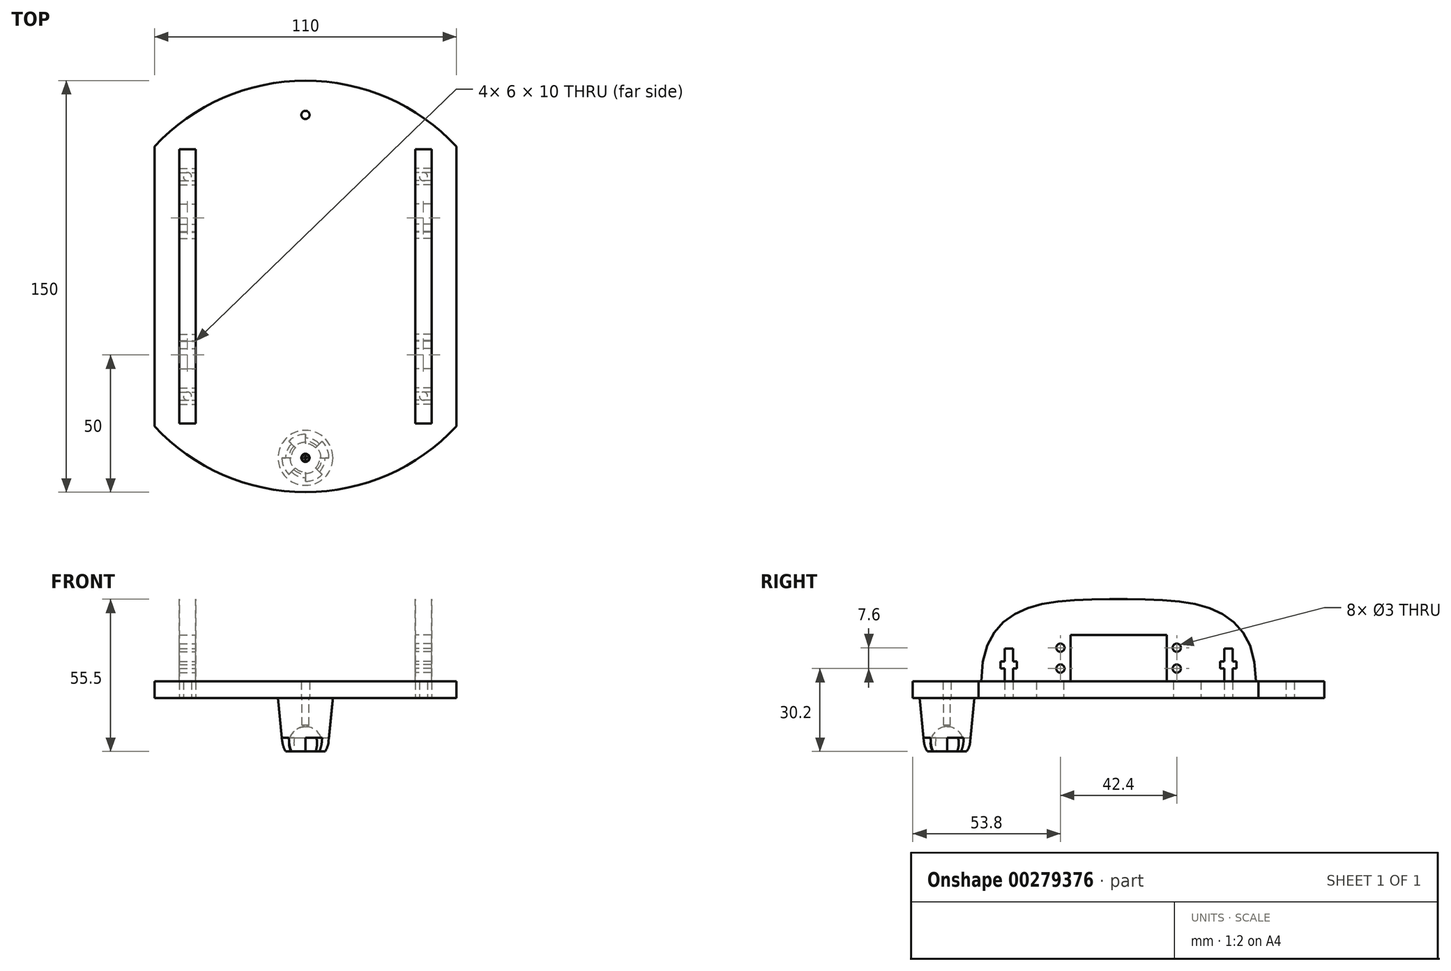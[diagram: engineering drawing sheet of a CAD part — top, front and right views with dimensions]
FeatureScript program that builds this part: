
annotation { "Feature Type Name" : "Feature", "Feature Type Description" : "" }
export const myFeature = defineFeature(function(context is Context, id is Id, definition is map)
    precondition{}
    {
        {
            var Q0;
            Q0=qCreatedBy(makeId("Top.planeOp"),FACE);
            var sketch = newSketch(context, id + "F0", { "sketchPlane" : qUnion([Q0])});
            skArc(sketch, "E0", {"start": v(55, 51) * mm, "mid": v(0, 75) * mm, "end": v(-55, 51) * mm});
            skLineSegment(sketch, "E1.bottom", {"start": v(40, 30) * mm, "end": v(46, 30) * mm});
            skLineSegment(sketch, "E1.top", {"start": v(40, 20) * mm, "end": v(46, 20) * mm});
            skLineSegment(sketch, "E1.left", {"start": v(40, 30) * mm, "end": v(40, 20) * mm});
            skLineSegment(sketch, "E1.right", {"start": v(46, 30) * mm, "end": v(46, 20) * mm});
            skLineSegment(sketch, "E2.MirrorCS", {"start": v(40, -30) * mm, "end": v(40, -20) * mm});
            skLineSegment(sketch, "E3.MirrorCS", {"start": v(40, -30) * mm, "end": v(46, -30) * mm});
            skLineSegment(sketch, "E4.MirrorCS", {"start": v(46, -30) * mm, "end": v(46, -20) * mm});
            skLineSegment(sketch, "E5.MirrorCS", {"start": v(40, -20) * mm, "end": v(46, -20) * mm});
            skLineSegment(sketch, "E6", {"start": v(55, 51) * mm, "end": v(55, -51) * mm});
            skLineSegment(sketch, "E7", {"start": v(43, -61.45) * mm, "end": v(43, 61.45) * mm, "construction": true});
            skPoint(sketch, "E7.startSnap0", {"position": v(43, -30) * mm});
            skCircle(sketch, "E8", {"center": v(43, -40) * mm, "radius": 1.5 * mm});
            skCircle(sketch, "E9.MirrorC", {"center": v(43, 40) * mm, "radius": 1.5 * mm});
            skCircle(sketch, "E10.MirrorC", {"center": v(-43, 40) * mm, "radius": 1.5 * mm});
            skLineSegment(sketch, "E11.MirrorCS", {"start": v(-40, -30) * mm, "end": v(-46, -30) * mm});
            skCircle(sketch, "E12.MirrorC", {"center": v(-43, -40) * mm, "radius": 1.5 * mm});
            skLineSegment(sketch, "E13.MirrorCS", {"start": v(-40, -20) * mm, "end": v(-46, -20) * mm});
            skPoint(sketch, "E14.MirrorP", {"position": v(-43, -30) * mm});
            skLineSegment(sketch, "E15.MirrorCS", {"start": v(-40, 30) * mm, "end": v(-46, 30) * mm});
            skLineSegment(sketch, "E16.MirrorCS", {"start": v(-40, -30) * mm, "end": v(-40, -20) * mm});
            skLineSegment(sketch, "E17.MirrorCS", {"start": v(-40, 30) * mm, "end": v(-40, 20) * mm});
            skLineSegment(sketch, "E18.MirrorCS", {"start": v(-40, 20) * mm, "end": v(-46, 20) * mm});
            skLineSegment(sketch, "E19.MirrorCS", {"start": v(-55, 51) * mm, "end": v(-55, -51) * mm});
            skLineSegment(sketch, "E20.MirrorCS", {"start": v(-46, 30) * mm, "end": v(-46, 20) * mm});
            skLineSegment(sketch, "E21.MirrorCS", {"start": v(-46, -30) * mm, "end": v(-46, -20) * mm});
            skArc(sketch, "E22.trimOffspring", {"start": v(-55, -51) * mm, "mid": v(0, -75) * mm, "end": v(55, -51) * mm});
            skCircle(sketch, "E23", {"center": v(0, -62.5) * mm, "radius": 1.5 * mm});
            skCircle(sketch, "E24.MirrorC", {"center": v(0, 62.5) * mm, "radius": 1.5 * mm});
            skSolve(sketch);
        }
        {
            var Q0;
            Q0 = qSketchRegion(id + "F0", true);
            extrude(context, id + "F1", {"entities" : qUnion([Q0]), "depth" : 6 * mm});
        }
        {
            var Q0;
            Q0=makeQuery(id+"F1.opExtrude","SWEPT_FACE",FACE,{"disambiguationData":[OSD([sQuery(id+"F0.wireOp",EDGE,"E1.left")])]});
            var sketch = newSketch(context, id + "F2", { "sketchPlane" : qUnion([Q0])});
            skLineSegment(sketch, "E25.0", {"start": v(-30, 0) * mm, "end": v(-20, 0) * mm});
            skLineSegment(sketch, "E26.0", {"start": v(-30, 6) * mm, "end": v(-30, 0) * mm});
            skLineSegment(sketch, "E27.0", {"start": v(-20, 6) * mm, "end": v(-20, 0) * mm});
            skLineSegment(sketch, "E28.0", {"start": v(20, 6) * mm, "end": v(20, 0) * mm});
            skLineSegment(sketch, "E29.0", {"start": v(30, 0) * mm, "end": v(20, 0) * mm});
            skLineSegment(sketch, "E30.0", {"start": v(30, 6) * mm, "end": v(30, 0) * mm});
            skLineSegment(sketch, "E31", {"start": v(-20, 6) * mm, "end": v(-17.5, 6) * mm});
            skLineSegment(sketch, "E32", {"start": v(-30, 6) * mm, "end": v(-38.5, 6) * mm});
            skLineSegment(sketch, "E33", {"start": v(30, 6) * mm, "end": v(38.5, 6) * mm});
            skFitSpline(sketch, "E34", {"points": [v(-50, 6) * mm, v(0, 36) * mm, v(50, 6) * mm], "startDerivative": vector(0, 180) * mm, "endDerivative": vector(0, -180) * mm});
            skLineSegment(sketch, "E35", {"start": v(-50, 6) * mm, "end": v(-50, 36) * mm, "construction": true});
            skLineSegment(sketch, "E36.top", {"start": v(17.5, 23) * mm, "end": v(-17.5, 23) * mm});
            skLineSegment(sketch, "E36.left", {"start": v(17.5, 6) * mm, "end": v(17.5, 23) * mm});
            skLineSegment(sketch, "E36.right", {"start": v(-17.5, 6) * mm, "end": v(-17.5, 23) * mm});
            skPoint(sketch, "E36.middle", {"position": v(0, 14.5) * mm});
            skLineSegment(sketch, "E37.trimOffspring", {"start": v(17.5, 6) * mm, "end": v(20, 6) * mm});
            skCircle(sketch, "E38", {"center": v(-21.2, 18.3) * mm, "radius": 1.5 * mm});
            skLineSegment(sketch, "E39", {"start": v(-17.5, 14.5) * mm, "end": v(17.5, 14.5) * mm, "construction": true});
            skCircle(sketch, "E40.MirrorC", {"center": v(21.2, 18.3) * mm, "radius": 1.5 * mm});
            skCircle(sketch, "E41.MirrorC", {"center": v(-21.2, 10.7) * mm, "radius": 1.5 * mm});
            skCircle(sketch, "E42.MirrorC", {"center": v(21.2, 10.7) * mm, "radius": 1.5 * mm});
            skLineSegment(sketch, "E43", {"start": v(-40, 6) * mm, "end": v(-40, 29.24) * mm, "construction": true});
            skLineSegment(sketch, "E44.top", {"start": v(-38.5, 18) * mm, "end": v(-41.5, 18) * mm});
            skLineSegment(sketch, "E44.left", {"start": v(-38.5, 6) * mm, "end": v(-38.5, 10.75) * mm});
            skLineSegment(sketch, "E44.right", {"start": v(-41.5, 6) * mm, "end": v(-41.5, 10.75) * mm});
            skPoint(sketch, "E44.middle", {"position": v(-40, 12) * mm});
            skLineSegment(sketch, "E45.bottom", {"start": v(-37, 10.75) * mm, "end": v(-38.5, 10.75) * mm});
            skLineSegment(sketch, "E45.top", {"start": v(-37, 13.25) * mm, "end": v(-38.5, 13.25) * mm});
            skLineSegment(sketch, "E45.left", {"start": v(-37, 10.75) * mm, "end": v(-37, 13.25) * mm});
            skLineSegment(sketch, "E45.right", {"start": v(-43, 10.75) * mm, "end": v(-43, 13.25) * mm});
            skLineSegment(sketch, "E46.trimOffspring", {"start": v(-41.5, 13.25) * mm, "end": v(-43, 13.25) * mm});
            skLineSegment(sketch, "E47.trimOffspring", {"start": v(-38.5, 13.25) * mm, "end": v(-38.5, 18) * mm});
            skLineSegment(sketch, "E48.trimOffspring", {"start": v(-41.5, 10.75) * mm, "end": v(-43, 10.75) * mm});
            skLineSegment(sketch, "E49.trimOffspring", {"start": v(-41.5, 13.25) * mm, "end": v(-41.5, 18) * mm});
            skLineSegment(sketch, "E50.trimOffspring", {"start": v(-41.5, 6) * mm, "end": v(-50, 6) * mm});
            skLineSegment(sketch, "E51.MirrorCS", {"start": v(43, 10.75) * mm, "end": v(43, 13.25) * mm});
            skLineSegment(sketch, "E52.MirrorCS", {"start": v(37, 13.25) * mm, "end": v(38.5, 13.25) * mm});
            skLineSegment(sketch, "E53.MirrorCS", {"start": v(37, 10.75) * mm, "end": v(37, 13.25) * mm});
            skLineSegment(sketch, "E54.MirrorCS", {"start": v(37, 10.75) * mm, "end": v(38.5, 10.75) * mm});
            skLineSegment(sketch, "E55.MirrorCS", {"start": v(41.5, 13.25) * mm, "end": v(43, 13.25) * mm});
            skLineSegment(sketch, "E56.MirrorCS", {"start": v(41.5, 10.75) * mm, "end": v(43, 10.75) * mm});
            skPoint(sketch, "E57.MirrorP", {"position": v(40, 12) * mm});
            skLineSegment(sketch, "E58.MirrorCS", {"start": v(38.5, 18) * mm, "end": v(41.5, 18) * mm});
            skLineSegment(sketch, "E59.MirrorCS", {"start": v(41.5, 6) * mm, "end": v(41.5, 10.75) * mm});
            skLineSegment(sketch, "E60.MirrorCS", {"start": v(41.5, 13.25) * mm, "end": v(41.5, 18) * mm});
            skLineSegment(sketch, "E61.MirrorCS", {"start": v(38.5, 6) * mm, "end": v(38.5, 10.75) * mm});
            skLineSegment(sketch, "E62.MirrorCS", {"start": v(38.5, 13.25) * mm, "end": v(38.5, 18) * mm});
            skLineSegment(sketch, "E63.trimOffspring", {"start": v(41.5, 6) * mm, "end": v(50, 6) * mm});
            skSolve(sketch);
        }
        {
            var Q0;
            Q0 = qSketchRegion(id + "F2", true);
            extrude(context, id + "F3", {"entities" : qUnion([Q0]), "depth" : 6 * mm});
        }
        {
            var Q0;
            Q0=makeQuery(id+"F3.opExtrude","SWEPT_BODY",BODY,{"disambiguationData":[OSD([sQuery(id+"F2.wireOp",EDGE,"E25.0"),sQuery(id+"F2.wireOp",EDGE,"E26.0"),sQuery(id+"F2.wireOp",EDGE,"E27.0"),sQuery(id+"F2.wireOp",EDGE,"E28.0"),sQuery(id+"F2.wireOp",EDGE,"E29.0"),sQuery(id+"F2.wireOp",EDGE,"E30.0"),sQuery(id+"F2.wireOp",EDGE,"E31"),sQuery(id+"F2.wireOp",EDGE,"E32"),sQuery(id+"F2.wireOp",EDGE,"E33"),sQuery(id+"F2.wireOp",EDGE,"E34"),sQuery(id+"F2.wireOp",EDGE,"E36.top"),sQuery(id+"F2.wireOp",EDGE,"E36.left"),sQuery(id+"F2.wireOp",EDGE,"E36.right"),sQuery(id+"F2.wireOp",EDGE,"E37.trimOffspring"),sQuery(id+"F2.wireOp",EDGE,"E38"),sQuery(id+"F2.wireOp",EDGE,"E40.MirrorC"),sQuery(id+"F2.wireOp",EDGE,"E41.MirrorC"),sQuery(id+"F2.wireOp",EDGE,"E42.MirrorC"),sQuery(id+"F2.wireOp",EDGE,"E44.top"),sQuery(id+"F2.wireOp",EDGE,"E44.left"),sQuery(id+"F2.wireOp",EDGE,"E44.right"),sQuery(id+"F2.wireOp",EDGE,"E45.bottom"),sQuery(id+"F2.wireOp",EDGE,"E45.top"),sQuery(id+"F2.wireOp",EDGE,"E45.left"),sQuery(id+"F2.wireOp",EDGE,"E45.right"),sQuery(id+"F2.wireOp",EDGE,"E46.trimOffspring"),sQuery(id+"F2.wireOp",EDGE,"E47.trimOffspring"),sQuery(id+"F2.wireOp",EDGE,"E48.trimOffspring"),sQuery(id+"F2.wireOp",EDGE,"E49.trimOffspring"),sQuery(id+"F2.wireOp",EDGE,"E50.trimOffspring"),sQuery(id+"F2.wireOp",EDGE,"E51.MirrorCS"),sQuery(id+"F2.wireOp",EDGE,"E52.MirrorCS"),sQuery(id+"F2.wireOp",EDGE,"E53.MirrorCS"),sQuery(id+"F2.wireOp",EDGE,"E54.MirrorCS"),sQuery(id+"F2.wireOp",EDGE,"E55.MirrorCS"),sQuery(id+"F2.wireOp",EDGE,"E56.MirrorCS"),sQuery(id+"F2.wireOp",EDGE,"E58.MirrorCS"),sQuery(id+"F2.wireOp",EDGE,"E59.MirrorCS"),sQuery(id+"F2.wireOp",EDGE,"E60.MirrorCS"),sQuery(id+"F2.wireOp",EDGE,"E61.MirrorCS"),sQuery(id+"F2.wireOp",EDGE,"E62.MirrorCS"),sQuery(id+"F2.wireOp",EDGE,"E63.trimOffspring")])]});
            var Q1;
            Q1=qCreatedBy(makeId("Right.planeOp"),FACE);
            mirror(context, id + "F4", {"entities" : qUnion([Q0]), "mirrorPlane" : qUnion([Q1])});
        }
        {
            var Q0;
            Q0=qCreatedBy(makeId("Right.planeOp"),FACE);
            var sketch = newSketch(context, id + "F5", { "sketchPlane" : qUnion([Q0])});
            skLineSegment(sketch, "E64", {"start": v(-72.5, 0) * mm, "end": v(-70.95, -15.83) * mm});
            skArc(sketch, "E65", {"start": v(-70.95, -15.83) * mm, "mid": v(-70.53, -17.74) * mm, "end": v(-69.7, -19.5) * mm});
            skPoint(sketch, "E66.0", {"position": v(-17.5, 14.5) * mm});
            skPoint(sketch, "E67.0", {"position": v(17.5, 14.5) * mm});
            skLineSegment(sketch, "E68", {"start": v(-17.5, 14.5) * mm, "end": v(17.5, 14.5) * mm, "construction": true});
            skPoint(sketch, "E69", {"position": v(0, 14.5) * mm});
            skCircle(sketch, "E70", {"center": v(0, 14.5) * mm, "radius": 37.5 * mm, "construction": true});
            skLineSegment(sketch, "E71", {"start": v(0, -23) * mm, "end": v(-75, -23) * mm, "construction": true});
            skLineSegment(sketch, "E72", {"start": v(-62.5, 0) * mm, "end": v(-62.5, -22) * mm});
            skLineSegment(sketch, "E73", {"start": v(-72.5, 0) * mm, "end": v(-62.5, 0) * mm});
            skArc(sketch, "E74", {"start": v(-62.5, -11) * mm, "mid": v(-68, -16.5) * mm, "end": v(-62.5, -22) * mm, "construction": true});
            skArc(sketch, "E75", {"start": v(-62.5, -10.5) * mm, "mid": v(-67.7, -13.5) * mm, "end": v(-67.7, -19.5) * mm});
            skLineSegment(sketch, "E76", {"start": v(-67.7, -19.5) * mm, "end": v(-69.7, -19.5) * mm});
            skSolve(sketch);
        }
        {
            var Q0;
            Q0=makeQuery(id+"F5.imprint","IMPRINT",FACE,{"disambiguationData":[TD([[makeQuery(id+"F5.imprint","IMPRINT",EDGE,{"derivedFrom":sQuery(id+"F5.wireOp",EDGE,"E64")}),1.0]])]});
            var Q1;
            Q1=sQuery(id+"F5.wireOp",EDGE,"E72");
            revolve(context, id + "F6", {"entities" : qUnion([Q0]), "axis" : qUnion([Q1]), "revolveType" : RevolveType.FULL});
        }
        {
            var Q0;
            Q0=makeQuery(id+"F6.opRevolve","SWEPT_FACE",FACE,{"disambiguationData":[OSD([sQuery(id+"F5.wireOp",EDGE,"E73")])]});
            var sketch = newSketch(context, id + "F7", { "sketchPlane" : qUnion([Q0])});
            skPoint(sketch, "E77", {"position": v(0, -62.5) * mm});
            skSolve(sketch);
        }
        {
            var Q0;
            Q0=sQuery(id+"F7.wireOp",VERTEX,"E77");
            var Q1;
            Q1=makeQuery(id+"F6.opRevolve","SWEPT_BODY",BODY,{"disambiguationData":[OSD([sQuery(id+"F5.wireOp",EDGE,"E64"),sQuery(id+"F5.wireOp",EDGE,"E65"),sQuery(id+"F5.wireOp",EDGE,"E72"),sQuery(id+"F5.wireOp",EDGE,"E73")])]});
            hole(context, id + "F8", {"style" : HoleStyle.SIMPLE, "endStyle" : HoleEndStyle.BLIND, "holeDiameter" : 2.5 * mm, "holeDepth" : 10 * mm, "isTappedThrough" : true, "tappedDepth" : 12 * mm, "tapClearance" : 3, "startFromSketch" : true, "locations" : qUnion([Q0]), "scope" : qUnion([Q1])});
        }
        {
            var Q0;
            Q0=makeQuery(id+"F6.opRevolve","SWEPT_FACE",FACE,{"disambiguationData":[OSD([sQuery(id+"F5.wireOp",EDGE,"E76")])]});
            var sketch = newSketch(context, id + "F9", { "sketchPlane" : qUnion([Q0])});
            skLineSegment(sketch, "E78", {"start": v(0, 62.5) * mm, "end": v(10, 62.5) * mm});
            skArc(sketch, "E79.0", {"start": v(10, 62.5) * mm, "mid": v(9.24, 58.67) * mm, "end": v(7.07, 55.43) * mm});
            skLineSegment(sketch, "E80", {"start": v(0, 62.5) * mm, "end": v(7.07, 55.43) * mm});
            skLineSegment(sketch, "E81.1.0", {"start": v(0, 62.5) * mm, "end": v(0, 72.5) * mm});
            skLineSegment(sketch, "E81.1.1", {"start": v(0, 62.5) * mm, "end": v(7.07, 69.57) * mm});
            skArc(sketch, "E81.1.2", {"start": v(0, 72.5) * mm, "mid": v(3.83, 71.74) * mm, "end": v(7.07, 69.57) * mm});
            skLineSegment(sketch, "E81.2.0", {"start": v(0, 62.5) * mm, "end": v(-10, 62.5) * mm});
            skLineSegment(sketch, "E81.2.1", {"start": v(0, 62.5) * mm, "end": v(-7.07, 69.57) * mm});
            skArc(sketch, "E81.2.2", {"start": v(-10, 62.5) * mm, "mid": v(-9.24, 66.33) * mm, "end": v(-7.07, 69.57) * mm});
            skLineSegment(sketch, "E81.3.0", {"start": v(0, 62.5) * mm, "end": v(0, 52.5) * mm});
            skLineSegment(sketch, "E81.3.1", {"start": v(0, 62.5) * mm, "end": v(-7.07, 55.43) * mm});
            skArc(sketch, "E81.3.2", {"start": v(0, 52.5) * mm, "mid": v(-3.83, 53.26) * mm, "end": v(-7.07, 55.43) * mm});
            skSolve(sketch);
        }
        {
            var Q0;
            Q0 = qSketchRegion(id + "F9", true);
            extrude(context, id + "F10", {"entities" : qUnion([Q0]), "operationType" : NewBodyOperationType.REMOVE, "oppositeDirection" : true, "depth" : 5 * mm});
        }
    });
